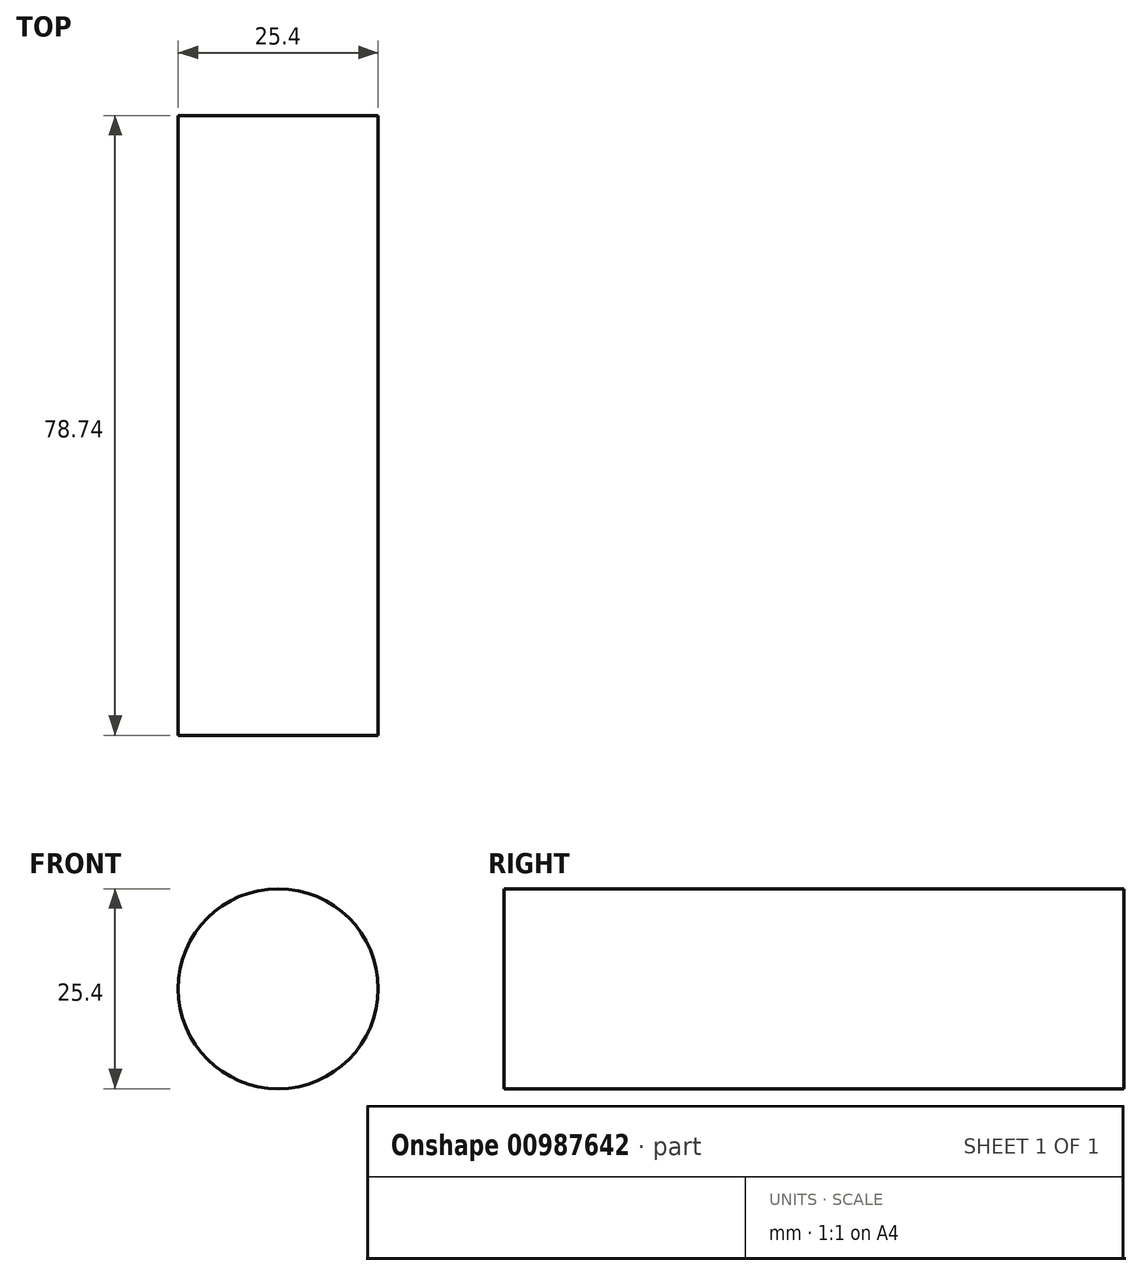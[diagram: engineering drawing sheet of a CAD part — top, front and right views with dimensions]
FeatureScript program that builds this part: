
annotation { "Feature Type Name" : "Feature", "Feature Type Description" : "" }
export const myFeature = defineFeature(function(context is Context, id is Id, definition is map)
    precondition{}
    {
        {
            var Q0;
            Q0=qCreatedBy(makeId("Front.planeOp"),FACE);
            var sketch = newSketch(context, id + "F0", { "sketchPlane" : qUnion([Q0])});
            skCircle(sketch, "E0", {"center": v(0, 0) * mm, "radius": 12.7 * mm});
            skSolve(sketch);
        }
        {
            var Q0;
            Q0=makeQuery(id+"F0.imprint","IMPRINT",FACE,{"disambiguationData":[TD([[makeQuery(id+"F0.imprint","IMPRINT",EDGE,{"derivedFrom":sQuery(id+"F0.wireOp",EDGE,"E0")}),1.0]])]});
            extrude(context, id + "F1", {"entities" : qUnion([Q0]), "depth" : 78.74 * mm, "offsetDistance" : 25.4 * mm});
        }
    });
